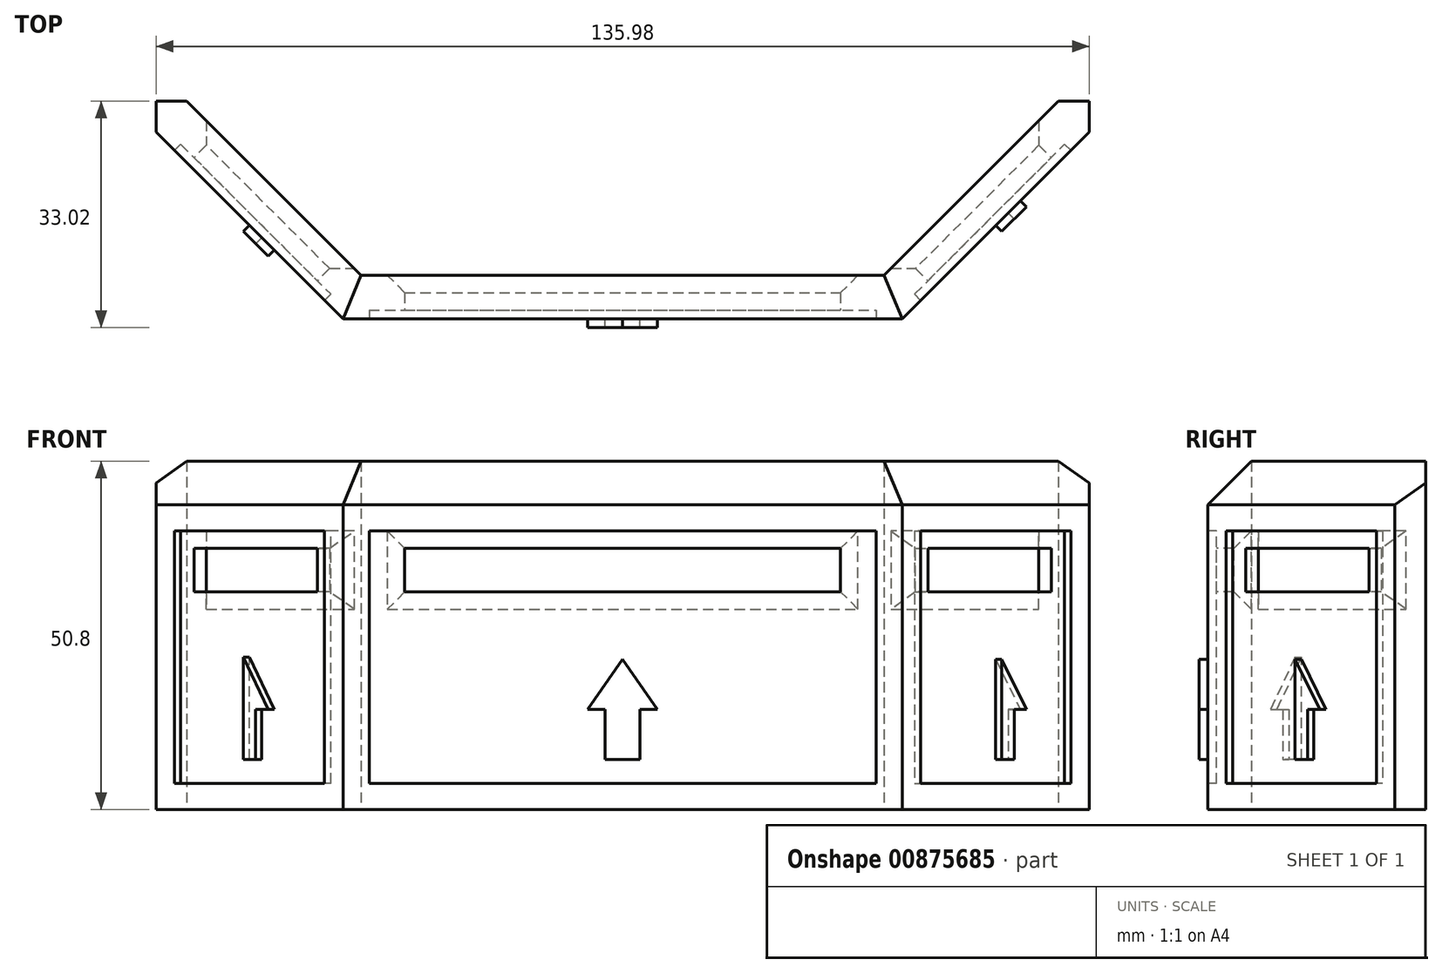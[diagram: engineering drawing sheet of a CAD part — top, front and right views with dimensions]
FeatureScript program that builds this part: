
annotation { "Feature Type Name" : "Feature", "Feature Type Description" : "" }
export const myFeature = defineFeature(function(context is Context, id is Id, definition is map)
    precondition{}
    {
        {
            var Q0;
            Q0=qCreatedBy(makeId("Top.planeOp"),FACE);
            var sketch = newSketch(context, id + "F0", { "sketchPlane" : qUnion([Q0])});
            skLineSegment(sketch, "E0", {"start": v(38.1, 0) * mm, "end": v(-38.1, 0) * mm});
            skLineSegment(sketch, "E1", {"start": v(-38.1, 0) * mm, "end": v(-63.5, 25.4) * mm});
            skLineSegment(sketch, "E2", {"start": v(38.1, 0) * mm, "end": v(63.5, 25.4) * mm});
            skPoint(sketch, "E3.start.orphan", {"position": v(0, 0) * mm});
            skLineSegment(sketch, "E4.0", {"start": v(42.6, -4.5) * mm, "end": v(68, 20.9) * mm});
            skLineSegment(sketch, "E5.0", {"start": v(-42.6, -4.5) * mm, "end": v(-68, 20.9) * mm});
            skLineSegment(sketch, "E6", {"start": v(-42.6, -4.5) * mm, "end": v(-40.73, -6.35) * mm});
            skLineSegment(sketch, "E7", {"start": v(-38.1, -6.35) * mm, "end": v(-40.73, -6.35) * mm});
            skLineSegment(sketch, "E8", {"start": v(-38.1, -6.35) * mm, "end": v(40.73, -6.35) * mm});
            skLineSegment(sketch, "E9", {"start": v(42.6, -4.5) * mm, "end": v(40.73, -6.35) * mm});
            skLineSegment(sketch, "E10", {"start": v(-68, 20.9) * mm, "end": v(-68, 25.4) * mm});
            skLineSegment(sketch, "E11", {"start": v(-63.5, 25.4) * mm, "end": v(-68, 25.4) * mm});
            skLineSegment(sketch, "E12", {"start": v(-68, 25.4) * mm, "end": v(-63.5, 25.4) * mm});
            skLineSegment(sketch, "E13", {"start": v(68, 20.9) * mm, "end": v(68, 25.4) * mm});
            skLineSegment(sketch, "E14.trimOffspring", {"start": v(63.5, 25.4) * mm, "end": v(68, 25.4) * mm});
            skSolve(sketch);
        }
        {
            var Q0;
            Q0 = qSketchRegion(id + "F0", true);
            extrude(context, id + "F1", {"entities" : qUnion([Q0]), "depth" : 50.8 * mm, "offsetDistance" : 25.4 * mm});
        }
        {
            var Q0;
            Q0=makeQuery(id+"F1.opExtrude","CAP_EDGE",EDGE,{"disambiguationData":[OSD([sQuery(id+"F0.wireOp",EDGE,"E5.0"),sQuery(id+"F0.wireOp",EDGE,"E6")])],"isStart":false});
            var Q1;
            Q1=makeQuery(id+"F1.opExtrude","CAP_EDGE",EDGE,{"disambiguationData":[OSD([sQuery(id+"F0.wireOp",EDGE,"E7"),sQuery(id+"F0.wireOp",EDGE,"E8")])],"isStart":false});
            var Q2;
            Q2=makeQuery(id+"F1.opExtrude","CAP_EDGE",EDGE,{"disambiguationData":[OSD([sQuery(id+"F0.wireOp",EDGE,"E4.0"),sQuery(id+"F0.wireOp",EDGE,"E9")])],"isStart":false});
            chamfer(context, id + "F2", {"entities" : qUnion([Q0, Q1, Q2]), "chamferType" : ChamferType.OFFSET_ANGLE, "width" : 6.35 * mm, "oppositeDirection" : false, "angle" : 45 * degree, "tangentPropagation" : true});
        }
        {
            var Q0;
            Q0=makeQuery(id+"F1.opExtrude","SWEPT_FACE",FACE,{"disambiguationData":[OSD([sQuery(id+"F0.wireOp",EDGE,"E7"),sQuery(id+"F0.wireOp",EDGE,"E8")])]});
            var sketch = newSketch(context, id + "F3", { "sketchPlane" : qUnion([Q0])});
            skLineSegment(sketch, "E15", {"start": v(0, 0) * mm, "end": v(0, 31.75) * mm});
            skLineSegment(sketch, "E16", {"start": v(0, 31.75) * mm, "end": v(31.75, 31.75) * mm});
            skLineSegment(sketch, "E17", {"start": v(31.75, 31.75) * mm, "end": v(-31.75, 31.75) * mm});
            skLineSegment(sketch, "E18", {"start": v(0, 31.75) * mm, "end": v(0, 38.1) * mm});
            skLineSegment(sketch, "E19", {"start": v(0, 38.1) * mm, "end": v(31.75, 38.1) * mm});
            skLineSegment(sketch, "E20", {"start": v(31.75, 38.1) * mm, "end": v(-31.75, 38.1) * mm});
            skLineSegment(sketch, "E21", {"start": v(-31.75, 31.75) * mm, "end": v(-31.75, 38.1) * mm});
            skLineSegment(sketch, "E22", {"start": v(31.75, 31.75) * mm, "end": v(31.75, 38.1) * mm});
            skLineSegment(sketch, "E23", {"start": v(0, 31.75) * mm, "end": v(0, 29.21) * mm});
            skLineSegment(sketch, "E24", {"start": v(0, 29.21) * mm, "end": v(0, 0) * mm});
            skLineSegment(sketch, "E25", {"start": v(0, 14.6) * mm, "end": v(0, 29.21) * mm});
            skLineSegment(sketch, "E26", {"start": v(0, 14.6) * mm, "end": v(0, 0) * mm});
            skLineSegment(sketch, "E27", {"start": v(0, 7.3) * mm, "end": v(-2.54, 7.3) * mm});
            skLineSegment(sketch, "E28", {"start": v(-2.54, 7.3) * mm, "end": v(2.54, 7.3) * mm});
            skLineSegment(sketch, "E29", {"start": v(-2.54, 14.6) * mm, "end": v(-5.08, 14.6) * mm});
            skLineSegment(sketch, "E30", {"start": v(2.54, 14.6) * mm, "end": v(5.08, 14.6) * mm});
            skLineSegment(sketch, "E31", {"start": v(-5.08, 14.6) * mm, "end": v(0, 21.9) * mm});
            skLineSegment(sketch, "E32", {"start": v(0, 21.9) * mm, "end": v(5.08, 14.6) * mm});
            skLineSegment(sketch, "E33", {"start": v(-2.54, 14.6) * mm, "end": v(-2.54, 7.3) * mm});
            skLineSegment(sketch, "E34", {"start": v(2.54, 14.6) * mm, "end": v(2.54, 7.3) * mm});
            skSolve(sketch);
        }
        {
            var Q0;
            {var subQ2=sQuery(id+"F3.wireOp",EDGE,"E18");Q0=makeQuery(id+"F3.imprint","IMPRINT",FACE,{"disambiguationData":[TD([[makeQuery(id+"F3.imprint","IMPRINT",EDGE,{"derivedFrom":subQ2}),-1.0]])]});}
            var Q1;
            {var subQ2=sQuery(id+"F3.wireOp",EDGE,"E18");Q1=makeQuery(id+"F3.imprint","IMPRINT",FACE,{"disambiguationData":[TD([[makeQuery(id+"F3.imprint","IMPRINT",EDGE,{"derivedFrom":subQ2}),1.0]])]});}
            extrude(context, id + "F4", {"entities" : qUnion([Q0, Q1]), "operationType" : NewBodyOperationType.REMOVE, "oppositeDirection" : true, "depth" : 25.4 * mm, "offsetDistance" : 25.4 * mm});
        }
        {
            var Q0;
            Q0=makeQuery(id+"F4.boolean.opBoolean","COPY",EDGE,{"derivedFrom":makeQuery(id+"F4.opExtrude","CAP_EDGE",EDGE,{"disambiguationData":[OSD([sQuery(id+"F3.wireOp",EDGE,"E17")])],"isStart":true})});
            var Q1;
            Q1=makeQuery(id+"F4.boolean.opBoolean","COPY",EDGE,{"derivedFrom":makeQuery(id+"F4.opExtrude","CAP_EDGE",EDGE,{"disambiguationData":[OSD([sQuery(id+"F3.wireOp",EDGE,"E21")])],"isStart":true})});
            var Q2;
            Q2=makeQuery(id+"F4.boolean.opBoolean","COPY",EDGE,{"derivedFrom":makeQuery(id+"F4.opExtrude","CAP_EDGE",EDGE,{"disambiguationData":[OSD([sQuery(id+"F3.wireOp",EDGE,"E20")])],"isStart":true})});
            var Q3;
            Q3=makeQuery(id+"F4.boolean.opBoolean","COPY",EDGE,{"derivedFrom":makeQuery(id+"F4.opExtrude","CAP_EDGE",EDGE,{"disambiguationData":[OSD([sQuery(id+"F3.wireOp",EDGE,"E22")])],"isStart":true})});
            var Q4;
            Q4=makeQuery(id+"F4.boolean.opBoolean","INTERSECT",EDGE,{"derivedFrom":[makeQuery(id+"F1.opExtrude","SWEPT_FACE",FACE,{"disambiguationData":[OSD([sQuery(id+"F0.wireOp",EDGE,"E0")])]}),makeQuery(id+"F4.opExtrude","SWEPT_FACE",FACE,{"disambiguationData":[OSD([sQuery(id+"F3.wireOp",EDGE,"E21")])]})]});
            var Q5;
            Q5=makeQuery(id+"F4.boolean.opBoolean","INTERSECT",EDGE,{"derivedFrom":[makeQuery(id+"F1.opExtrude","SWEPT_FACE",FACE,{"disambiguationData":[OSD([sQuery(id+"F0.wireOp",EDGE,"E0")])]}),makeQuery(id+"F4.opExtrude","SWEPT_FACE",FACE,{"disambiguationData":[OSD([sQuery(id+"F3.wireOp",EDGE,"E20")])]})]});
            var Q6;
            Q6=makeQuery(id+"F4.boolean.opBoolean","INTERSECT",EDGE,{"derivedFrom":[makeQuery(id+"F1.opExtrude","SWEPT_FACE",FACE,{"disambiguationData":[OSD([sQuery(id+"F0.wireOp",EDGE,"E0")])]}),makeQuery(id+"F4.opExtrude","SWEPT_FACE",FACE,{"disambiguationData":[OSD([sQuery(id+"F3.wireOp",EDGE,"E17")])]})]});
            var Q7;
            Q7=makeQuery(id+"F4.boolean.opBoolean","INTERSECT",EDGE,{"derivedFrom":[makeQuery(id+"F1.opExtrude","SWEPT_FACE",FACE,{"disambiguationData":[OSD([sQuery(id+"F0.wireOp",EDGE,"E0")])]}),makeQuery(id+"F4.opExtrude","SWEPT_FACE",FACE,{"disambiguationData":[OSD([sQuery(id+"F3.wireOp",EDGE,"E22")])]})]});
            chamfer(context, id + "F5", {"entities" : qUnion([Q0, Q1, Q2, Q3, Q4, Q5, Q6, Q7]), "width" : 2.54 * mm, "tangentPropagation" : true});
        }
        {
            var Q0;
            Q0=makeQuery(id+"F1.opExtrude","SWEPT_FACE",FACE,{"disambiguationData":[OSD([sQuery(id+"F0.wireOp",EDGE,"E5.0"),sQuery(id+"F0.wireOp",EDGE,"E6")])]});
            var sketch = newSketch(context, id + "F6", { "sketchPlane" : qUnion([Q0])});
            skLineSegment(sketch, "E35", {"start": v(-47.4, 31.75) * mm, "end": v(-30.89, 31.75) * mm});
            skLineSegment(sketch, "E36", {"start": v(-30.89, 31.75) * mm, "end": v(-56.29, 31.75) * mm});
            skLineSegment(sketch, "E37", {"start": v(-30.89, 31.75) * mm, "end": v(-30.89, 38.1) * mm});
            skLineSegment(sketch, "E38", {"start": v(-39.78, 38.1) * mm, "end": v(-30.89, 38.1) * mm});
            skLineSegment(sketch, "E39", {"start": v(-30.89, 38.1) * mm, "end": v(-56.29, 38.1) * mm});
            skLineSegment(sketch, "E40", {"start": v(-56.29, 31.75) * mm, "end": v(-56.29, 38.1) * mm});
            skPoint(sketch, "E41.start.orphan", {"position": v(-43.59, 0) * mm});
            skLineSegment(sketch, "E42", {"start": v(-43.59, 0) * mm, "end": v(-43.59, 44.45) * mm});
            skLineSegment(sketch, "E43", {"start": v(-43.59, 44.45) * mm, "end": v(-43.59, 31.75) * mm});
            skLineSegment(sketch, "E44", {"start": v(-43.59, 31.75) * mm, "end": v(-43.59, 29.21) * mm});
            skLineSegment(sketch, "E45", {"start": v(-43.59, 29.21) * mm, "end": v(-43.59, 0) * mm});
            skLineSegment(sketch, "E46", {"start": v(-43.59, 14.6) * mm, "end": v(-43.59, 29.21) * mm});
            skLineSegment(sketch, "E47", {"start": v(-43.59, 14.6) * mm, "end": v(-43.59, 0) * mm});
            skLineSegment(sketch, "E48", {"start": v(-46.13, 14.6) * mm, "end": v(-48.67, 14.6) * mm});
            skLineSegment(sketch, "E49", {"start": v(-48.67, 14.6) * mm, "end": v(-46.13, 14.6) * mm});
            skLineSegment(sketch, "E50", {"start": v(-43.59, 22.23) * mm, "end": v(-48.67, 14.6) * mm});
            skLineSegment(sketch, "E51", {"start": v(-43.59, 22.23) * mm, "end": v(-38.5, 14.6) * mm});
            skLineSegment(sketch, "E52", {"start": v(-46.13, 14.6) * mm, "end": v(-46.13, 7.3) * mm});
            skLineSegment(sketch, "E53", {"start": v(-38.5, 14.6) * mm, "end": v(-41.05, 14.6) * mm});
            skLineSegment(sketch, "E54", {"start": v(-41.05, 14.6) * mm, "end": v(-41.05, 7.3) * mm});
            skLineSegment(sketch, "E55", {"start": v(-43.59, 7.3) * mm, "end": v(-41.05, 7.3) * mm});
            skLineSegment(sketch, "E56", {"start": v(-41.05, 7.3) * mm, "end": v(-46.13, 7.3) * mm});
            skLineSegment(sketch, "E57.trimOffspring", {"start": v(-41.05, 14.6) * mm, "end": v(-38.5, 14.6) * mm});
            skSolve(sketch);
        }
        {
            var Q0;
            {var subQ1=sQuery(id+"F6.wireOp",EDGE,"E37");Q0=makeQuery(id+"F6.imprint","IMPRINT",FACE,{"disambiguationData":[TD([[makeQuery(id+"F6.imprint","IMPRINT",EDGE,{"derivedFrom":subQ1}),1.0]])]});}
            var Q1;
            {var subQ0=sQuery(id+"F6.wireOp",EDGE,"E40");Q1=makeQuery(id+"F6.imprint","IMPRINT",FACE,{"disambiguationData":[TD([[makeQuery(id+"F6.imprint","IMPRINT",EDGE,{"derivedFrom":subQ0}),-1.0]])]});}
            extrude(context, id + "F7", {"entities" : qUnion([Q0, Q1]), "operationType" : NewBodyOperationType.REMOVE, "oppositeDirection" : true, "depth" : 25.4 * mm, "offsetDistance" : 25.4 * mm});
        }
        {
            var Q0;
            Q0=makeQuery(id+"F7.boolean.opBoolean","COPY",EDGE,{"derivedFrom":makeQuery(id+"F7.opExtrude","CAP_EDGE",EDGE,{"disambiguationData":[OSD([sQuery(id+"F6.wireOp",EDGE,"E39")])],"isStart":true})});
            var Q1;
            Q1=makeQuery(id+"F7.boolean.opBoolean","COPY",EDGE,{"derivedFrom":makeQuery(id+"F7.opExtrude","CAP_EDGE",EDGE,{"disambiguationData":[OSD([sQuery(id+"F6.wireOp",EDGE,"E37")])],"isStart":true})});
            var Q2;
            Q2=makeQuery(id+"F7.boolean.opBoolean","COPY",EDGE,{"derivedFrom":makeQuery(id+"F7.opExtrude","CAP_EDGE",EDGE,{"disambiguationData":[OSD([sQuery(id+"F6.wireOp",EDGE,"E36")])],"isStart":true})});
            var Q3;
            Q3=makeQuery(id+"F7.boolean.opBoolean","COPY",EDGE,{"derivedFrom":makeQuery(id+"F7.opExtrude","CAP_EDGE",EDGE,{"disambiguationData":[OSD([sQuery(id+"F6.wireOp",EDGE,"E40")])],"isStart":true})});
            var Q4;
            Q4=makeQuery(id+"F7.boolean.opBoolean","INTERSECT",EDGE,{"derivedFrom":[makeQuery(id+"F1.opExtrude","SWEPT_FACE",FACE,{"disambiguationData":[OSD([sQuery(id+"F0.wireOp",EDGE,"E1")])]}),makeQuery(id+"F7.opExtrude","SWEPT_FACE",FACE,{"disambiguationData":[OSD([sQuery(id+"F6.wireOp",EDGE,"E39")])]})]});
            var Q5;
            Q5=makeQuery(id+"F7.boolean.opBoolean","INTERSECT",EDGE,{"derivedFrom":[makeQuery(id+"F1.opExtrude","SWEPT_FACE",FACE,{"disambiguationData":[OSD([sQuery(id+"F0.wireOp",EDGE,"E1")])]}),makeQuery(id+"F7.opExtrude","SWEPT_FACE",FACE,{"disambiguationData":[OSD([sQuery(id+"F6.wireOp",EDGE,"E37")])]})]});
            var Q6;
            Q6=makeQuery(id+"F7.boolean.opBoolean","INTERSECT",EDGE,{"derivedFrom":[makeQuery(id+"F1.opExtrude","SWEPT_FACE",FACE,{"disambiguationData":[OSD([sQuery(id+"F0.wireOp",EDGE,"E1")])]}),makeQuery(id+"F7.opExtrude","SWEPT_FACE",FACE,{"disambiguationData":[OSD([sQuery(id+"F6.wireOp",EDGE,"E36")])]})]});
            var Q7;
            Q7=makeQuery(id+"F7.boolean.opBoolean","INTERSECT",EDGE,{"derivedFrom":[makeQuery(id+"F1.opExtrude","SWEPT_FACE",FACE,{"disambiguationData":[OSD([sQuery(id+"F0.wireOp",EDGE,"E1")])]}),makeQuery(id+"F7.opExtrude","SWEPT_FACE",FACE,{"disambiguationData":[OSD([sQuery(id+"F6.wireOp",EDGE,"E40")])]})]});
            chamfer(context, id + "F8", {"entities" : qUnion([Q0, Q1, Q2, Q3, Q4, Q5, Q6, Q7]), "width" : 2.54 * mm, "tangentPropagation" : true});
        }
        {
            var Q0;
            Q0=makeQuery(id+"F1.opExtrude","SWEPT_FACE",FACE,{"disambiguationData":[OSD([sQuery(id+"F0.wireOp",EDGE,"E4.0"),sQuery(id+"F0.wireOp",EDGE,"E9")])]});
            var sketch = newSketch(context, id + "F9", { "sketchPlane" : qUnion([Q0])});
            skLineSegment(sketch, "E58", {"start": v(30.89, 31.75) * mm, "end": v(56.29, 31.75) * mm});
            skLineSegment(sketch, "E59", {"start": v(43.59, 38.1) * mm, "end": v(56.29, 38.1) * mm});
            skLineSegment(sketch, "E60", {"start": v(56.29, 38.1) * mm, "end": v(30.89, 38.1) * mm});
            skLineSegment(sketch, "E61", {"start": v(30.89, 31.75) * mm, "end": v(30.89, 38.1) * mm});
            skLineSegment(sketch, "E62", {"start": v(56.29, 31.75) * mm, "end": v(56.29, 38.1) * mm});
            skPoint(sketch, "E63.end.orphan", {"position": v(43.59, 31.75) * mm});
            skPoint(sketch, "E63.start.orphan", {"position": v(43.59, 0) * mm});
            skLineSegment(sketch, "E64", {"start": v(43.59, 0) * mm, "end": v(43.59, 44.45) * mm});
            skLineSegment(sketch, "E65", {"start": v(43.59, 44.45) * mm, "end": v(43.59, 31.75) * mm});
            skLineSegment(sketch, "E66", {"start": v(43.59, 31.75) * mm, "end": v(43.59, 29.21) * mm});
            skLineSegment(sketch, "E67", {"start": v(43.59, 29.21) * mm, "end": v(43.59, 0) * mm});
            skLineSegment(sketch, "E68", {"start": v(43.59, 14.6) * mm, "end": v(43.59, 29.21) * mm});
            skLineSegment(sketch, "E69", {"start": v(43.59, 14.6) * mm, "end": v(43.59, 0) * mm});
            skLineSegment(sketch, "E70", {"start": v(41.05, 14.6) * mm, "end": v(38.5, 14.6) * mm});
            skLineSegment(sketch, "E71", {"start": v(38.5, 14.6) * mm, "end": v(41.05, 14.6) * mm});
            skLineSegment(sketch, "E72", {"start": v(43.59, 21.9) * mm, "end": v(38.5, 14.6) * mm});
            skLineSegment(sketch, "E73", {"start": v(43.59, 21.9) * mm, "end": v(48.67, 14.6) * mm});
            skLineSegment(sketch, "E74", {"start": v(41.05, 14.6) * mm, "end": v(41.05, 7.3) * mm});
            skLineSegment(sketch, "E75", {"start": v(46.13, 14.6) * mm, "end": v(48.67, 14.6) * mm});
            skLineSegment(sketch, "E76", {"start": v(46.13, 14.6) * mm, "end": v(46.13, 7.3) * mm});
            skLineSegment(sketch, "E77", {"start": v(43.59, 7.3) * mm, "end": v(46.13, 7.3) * mm});
            skLineSegment(sketch, "E78", {"start": v(46.13, 7.3) * mm, "end": v(41.05, 7.3) * mm});
            skPoint(sketch, "E79.orphan", {"position": v(41.05, 6.33) * mm});
            skSolve(sketch);
        }
        {
            var Q0;
            {var subQ0=sQuery(id+"F9.wireOp",EDGE,"E61");Q0=makeQuery(id+"F9.imprint","IMPRINT",FACE,{"disambiguationData":[TD([[makeQuery(id+"F9.imprint","IMPRINT",EDGE,{"derivedFrom":subQ0}),-1.0]])]});}
            var Q1;
            {var subQ0=sQuery(id+"F9.wireOp",EDGE,"E62");Q1=makeQuery(id+"F9.imprint","IMPRINT",FACE,{"disambiguationData":[TD([[makeQuery(id+"F9.imprint","IMPRINT",EDGE,{"derivedFrom":subQ0}),1.0]])]});}
            extrude(context, id + "F10", {"entities" : qUnion([Q0, Q1]), "operationType" : NewBodyOperationType.REMOVE, "oppositeDirection" : true, "depth" : 25.4 * mm, "offsetDistance" : 25.4 * mm});
        }
        {
            var Q0;
            Q0=makeQuery(id+"F10.boolean.opBoolean","COPY",EDGE,{"derivedFrom":makeQuery(id+"F10.opExtrude","CAP_EDGE",EDGE,{"disambiguationData":[OSD([sQuery(id+"F9.wireOp",EDGE,"E60")])],"isStart":true})});
            var Q1;
            Q1=makeQuery(id+"F10.boolean.opBoolean","COPY",EDGE,{"derivedFrom":makeQuery(id+"F10.opExtrude","CAP_EDGE",EDGE,{"disambiguationData":[OSD([sQuery(id+"F9.wireOp",EDGE,"E61")])],"isStart":true})});
            var Q2;
            Q2=makeQuery(id+"F10.boolean.opBoolean","COPY",EDGE,{"derivedFrom":makeQuery(id+"F10.opExtrude","CAP_EDGE",EDGE,{"disambiguationData":[OSD([sQuery(id+"F9.wireOp",EDGE,"E58")])],"isStart":true})});
            var Q3;
            Q3=makeQuery(id+"F10.boolean.opBoolean","COPY",EDGE,{"derivedFrom":makeQuery(id+"F10.opExtrude","CAP_EDGE",EDGE,{"disambiguationData":[OSD([sQuery(id+"F9.wireOp",EDGE,"E62")])],"isStart":true})});
            var Q4;
            Q4=makeQuery(id+"F10.boolean.opBoolean","INTERSECT",EDGE,{"derivedFrom":[makeQuery(id+"F1.opExtrude","SWEPT_FACE",FACE,{"disambiguationData":[OSD([sQuery(id+"F0.wireOp",EDGE,"E2")])]}),makeQuery(id+"F10.opExtrude","SWEPT_FACE",FACE,{"disambiguationData":[OSD([sQuery(id+"F9.wireOp",EDGE,"E61")])]})]});
            var Q5;
            Q5=makeQuery(id+"F10.boolean.opBoolean","INTERSECT",EDGE,{"derivedFrom":[makeQuery(id+"F1.opExtrude","SWEPT_FACE",FACE,{"disambiguationData":[OSD([sQuery(id+"F0.wireOp",EDGE,"E2")])]}),makeQuery(id+"F10.opExtrude","SWEPT_FACE",FACE,{"disambiguationData":[OSD([sQuery(id+"F9.wireOp",EDGE,"E60")])]})]});
            var Q6;
            Q6=makeQuery(id+"F10.boolean.opBoolean","INTERSECT",EDGE,{"derivedFrom":[makeQuery(id+"F1.opExtrude","SWEPT_FACE",FACE,{"disambiguationData":[OSD([sQuery(id+"F0.wireOp",EDGE,"E2")])]}),makeQuery(id+"F10.opExtrude","SWEPT_FACE",FACE,{"disambiguationData":[OSD([sQuery(id+"F9.wireOp",EDGE,"E58")])]})]});
            var Q7;
            Q7=makeQuery(id+"F10.boolean.opBoolean","INTERSECT",EDGE,{"derivedFrom":[makeQuery(id+"F1.opExtrude","SWEPT_FACE",FACE,{"disambiguationData":[OSD([sQuery(id+"F0.wireOp",EDGE,"E2")])]}),makeQuery(id+"F10.opExtrude","SWEPT_FACE",FACE,{"disambiguationData":[OSD([sQuery(id+"F9.wireOp",EDGE,"E62")])]})]});
            chamfer(context, id + "F11", {"entities" : qUnion([Q0, Q1, Q2, Q3, Q4, Q5, Q6, Q7]), "width" : 2.54 * mm, "tangentPropagation" : true});
        }
        {
            var Q0;
            Q0=makeQuery(id+"F1.opExtrude","SWEPT_FACE",FACE,{"disambiguationData":[OSD([sQuery(id+"F0.wireOp",EDGE,"E7"),sQuery(id+"F0.wireOp",EDGE,"E8")])]});
            var sketch = newSketch(context, id + "F12", { "sketchPlane" : qUnion([Q0])});
            skLineSegment(sketch, "E80.0", {"start": v(36.92, 3.81) * mm, "end": v(36.92, 40.64) * mm});
            skLineSegment(sketch, "E80.1", {"start": v(-36.92, 3.81) * mm, "end": v(36.92, 3.81) * mm});
            skLineSegment(sketch, "E80.2", {"start": v(-36.92, 40.64) * mm, "end": v(-36.92, 3.81) * mm});
            skLineSegment(sketch, "E80.3", {"start": v(36.92, 40.64) * mm, "end": v(-36.92, 40.64) * mm});
            skSolve(sketch);
        }
        {
            var Q0;
            Q0=makeQuery(id+"F1.opExtrude","SWEPT_FACE",FACE,{"disambiguationData":[OSD([sQuery(id+"F0.wireOp",EDGE,"E5.0"),sQuery(id+"F0.wireOp",EDGE,"E6")])]});
            var sketch = newSketch(context, id + "F13", { "sketchPlane" : qUnion([Q0])});
            skLineSegment(sketch, "E81.0", {"start": v(-28.12, 3.81) * mm, "end": v(-28.12, 40.64) * mm});
            skLineSegment(sketch, "E81.1", {"start": v(-59.05, 3.81) * mm, "end": v(-28.12, 3.81) * mm});
            skLineSegment(sketch, "E81.2", {"start": v(-59.05, 40.64) * mm, "end": v(-59.05, 3.81) * mm});
            skLineSegment(sketch, "E81.3", {"start": v(-28.12, 40.64) * mm, "end": v(-59.05, 40.64) * mm});
            skSolve(sketch);
        }
        {
            var Q0;
            Q0=makeQuery(id+"F1.opExtrude","SWEPT_FACE",FACE,{"disambiguationData":[OSD([sQuery(id+"F0.wireOp",EDGE,"E4.0"),sQuery(id+"F0.wireOp",EDGE,"E9")])]});
            var sketch = newSketch(context, id + "F14", { "sketchPlane" : qUnion([Q0])});
            skLineSegment(sketch, "E82.0", {"start": v(59.05, 3.81) * mm, "end": v(59.05, 40.64) * mm});
            skLineSegment(sketch, "E82.1", {"start": v(28.12, 3.81) * mm, "end": v(59.05, 3.81) * mm});
            skLineSegment(sketch, "E82.2", {"start": v(28.12, 40.64) * mm, "end": v(28.12, 3.81) * mm});
            skLineSegment(sketch, "E82.3", {"start": v(59.05, 40.64) * mm, "end": v(28.12, 40.64) * mm});
            skSolve(sketch);
        }
        {
            var Q0;
            {var subQ4=sQuery(id+"F12.wireOp",EDGE,"E80.0");Q0=makeQuery(id+"F12.imprint","IMPRINT",FACE,{"disambiguationData":[TD([[makeQuery(id+"F12.imprint","IMPRINT",EDGE,{"derivedFrom":subQ4}),1.0]])]});}
            extrude(context, id + "F15", {"entities" : qUnion([Q0]), "operationType" : NewBodyOperationType.REMOVE, "oppositeDirection" : true, "depth" : 1.27 * mm, "offsetDistance" : 25.4 * mm});
        }
        {
            var Q0;
            {var subQ3=sQuery(id+"F13.wireOp",EDGE,"E81.0");Q0=makeQuery(id+"F13.imprint","IMPRINT",FACE,{"disambiguationData":[TD([[makeQuery(id+"F13.imprint","IMPRINT",EDGE,{"derivedFrom":subQ3}),1.0]])]});}
            extrude(context, id + "F16", {"entities" : qUnion([Q0]), "operationType" : NewBodyOperationType.REMOVE, "oppositeDirection" : true, "depth" : 1.27 * mm, "offsetDistance" : 25.4 * mm});
        }
        {
            var Q0;
            {var subQ3=sQuery(id+"F14.wireOp",EDGE,"E82.0");Q0=makeQuery(id+"F14.imprint","IMPRINT",FACE,{"disambiguationData":[TD([[makeQuery(id+"F14.imprint","IMPRINT",EDGE,{"derivedFrom":subQ3}),1.0]])]});}
            extrude(context, id + "F17", {"entities" : qUnion([Q0]), "operationType" : NewBodyOperationType.REMOVE, "oppositeDirection" : true, "depth" : 1.27 * mm, "offsetDistance" : 25.4 * mm});
        }
        {
            var Q0;
            Q0=makeQuery(id+"F3.imprint","IMPRINT",FACE,{"disambiguationData":[TD([[makeQuery(id+"F3.imprint","IMPRINT",EDGE,{"derivedFrom":sQuery(id+"F3.wireOp",EDGE,"E30")}),1.0]])]});
            var Q1;
            Q1=makeQuery(id+"F3.imprint","IMPRINT",FACE,{"disambiguationData":[TD([[makeQuery(id+"F3.imprint","IMPRINT",EDGE,{"derivedFrom":sQuery(id+"F3.wireOp",EDGE,"E29")}),-1.0]])]});
            extrude(context, id + "F18", {"entities" : qUnion([Q0, Q1]), "depth" : 1.27 * mm, "offsetDistance" : 25.4 * mm});
        }
        {
            var Q0;
            {var subQ1=sQuery(id+"F9.wireOp",EDGE,"E73");Q0=makeQuery(id+"F9.imprint","IMPRINT",FACE,{"disambiguationData":[TD([[makeQuery(id+"F9.imprint","IMPRINT",EDGE,{"derivedFrom":subQ1}),-1.0]])]});}
            var Q1;
            Q1=makeQuery(id+"F9.imprint","IMPRINT",FACE,{"disambiguationData":[TD([[makeQuery(id+"F9.imprint","IMPRINT",EDGE,{"derivedFrom":sQuery(id+"F9.wireOp",EDGE,"E71")}),1.0]])]});
            extrude(context, id + "F19", {"entities" : qUnion([Q0, Q1]), "depth" : 1.27 * mm, "offsetDistance" : 25.4 * mm});
        }
        {
            var Q0;
            {var subQ1=sQuery(id+"F6.wireOp",EDGE,"E51");Q0=makeQuery(id+"F6.imprint","IMPRINT",FACE,{"disambiguationData":[TD([[makeQuery(id+"F6.imprint","IMPRINT",EDGE,{"derivedFrom":subQ1}),-1.0]])]});}
            var Q1;
            Q1=makeQuery(id+"F6.imprint","IMPRINT",FACE,{"disambiguationData":[TD([[makeQuery(id+"F6.imprint","IMPRINT",EDGE,{"derivedFrom":sQuery(id+"F6.wireOp",EDGE,"E49")}),1.0]])]});
            extrude(context, id + "F20", {"entities" : qUnion([Q0, Q1]), "depth" : 1.27 * mm, "offsetDistance" : 25.4 * mm});
        }
    });
